# Revit family: KKU-RLT-KIT450VJ2
name_source: partatom
category: HLS-Bauteile
revit_build: Autodesk Revit 2016 (Build: 20150714_1515(x64)
units: mm (PartAtom-declared; Revit-internal decimal feet)

## family parameters
Arbeitsebenenbasiert = Nein
Beim Laden mit Abzugskörper schneiden = Nein
Bemaßung runder Anschluss = Durchmesser verwenden
Gemeinsam genutzt = Nein
Immer vertikal = Ja
OmniClass-Nummer = 23.85.80.11
OmniClass-Titel = Building Controls
Raumberechnungspunkt = Nein
Teiletyp = Normal

## types (1)
- KKU-RLT-KIT450VJ2
    ALG_Absicherung_in_A = 6
    ALG_Gewicht_in_kg = 10
    ALG_Info-Rohranschlüsse = Sauggas-/Flüssigkeitsleitung DN35/DN18
    ALG_ManufacturerCode = RLT-KIT450VJ2
    ALG_Schutzklasse = IP 54
    ALG_Umgebungsbedingungen = -20 bis 35 °C
    Beschreibung = Lüftungskit
    HLS_Bezeichnung_1 = RLT-KIT450VJ2
    HLS_Breite = 150 mm
    HLS_Höhe = 500 mm  [stored 1.64042 ft]
    HLS_Länge = 500 mm  [stored 1.64042 ft]
    HLS_Typ = RLT-KIT450VJ2
    Heizleistung = 53 kW
    Hersteller = YANMAR
    Kühlleistung = 45 kW
    Modell = RLT-KIT450VJ2
    Typenkommentare = Lüftungskit
    URL = www.energysystem-yanmar.com

note: [stored X ft] marks values corroborated as IEEE doubles in the binary element streams (Revit-internal decimal feet)

## geometry (parser evidence)
native form markers: Blend x9, Sweep x3
no freeform markers — native parametric forms only
